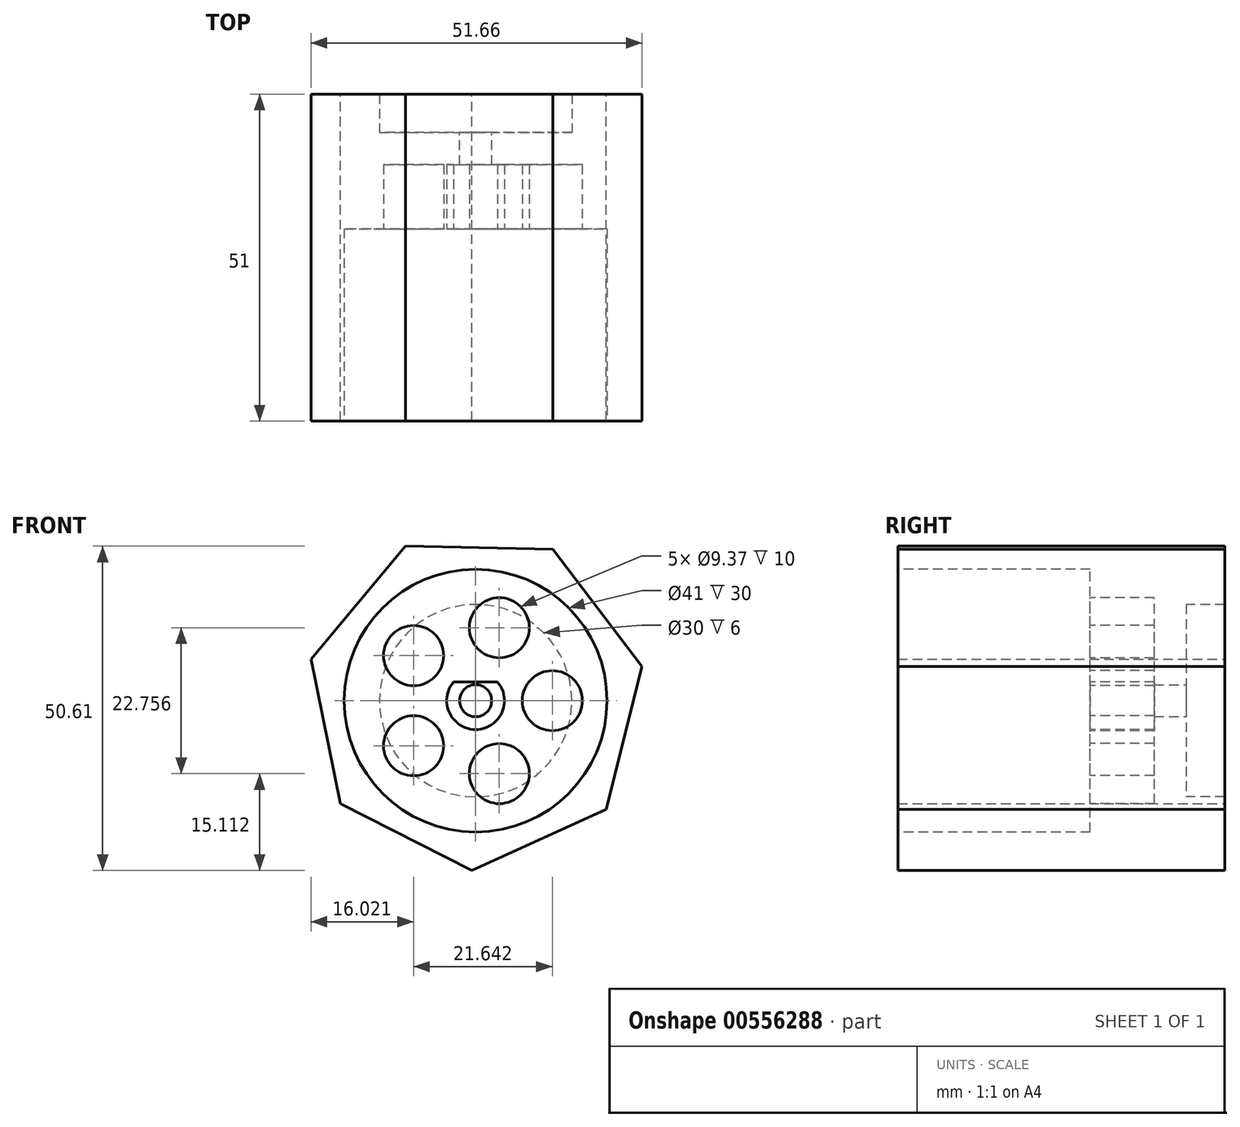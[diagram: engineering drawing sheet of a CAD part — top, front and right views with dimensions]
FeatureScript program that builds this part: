
annotation { "Feature Type Name" : "Feature", "Feature Type Description" : "" }
export const myFeature = defineFeature(function(context is Context, id is Id, definition is map)
    precondition{}
    {
        {
            var Q0;
            Q0=qCreatedBy(makeId("Front.planeOp"),FACE);
            var sketch = newSketch(context, id + "F0", { "sketchPlane" : qUnion([Q0])});
            skCircle(sketch, "E0", {"center": v(0, 0) * mm, "radius": 26.5 * mm});
            skSolve(sketch);
        }
        {
            var Q0;
            Q0 = qSketchRegion(id + "F0", true);
            extrude(context, id + "F1", {"entities" : qUnion([Q0]), "depth" : 45 * mm, "offsetDistance" : 25 * mm});
        }
        {
            var Q0;
            Q0=makeQuery(id+"F1.opExtrude","CAP_FACE",FACE,{"disambiguationData":[OSD([sQuery(id+"F0.wireOp",EDGE,"E0")])],"isStart":false});
            var sketch = newSketch(context, id + "F2", { "sketchPlane" : qUnion([Q0])});
            skCircle(sketch, "E1", {"center": v(0, 0) * mm, "radius": 20.5 * mm});
            skSolve(sketch);
        }
        {
            var Q0;
            Q0 = qSketchRegion(id + "F2", true);
            extrude(context, id + "F3", {"entities" : qUnion([Q0]), "operationType" : NewBodyOperationType.REMOVE, "oppositeDirection" : true, "depth" : 30 * mm, "offsetDistance" : 25 * mm});
        }
        {
            var Q0;
            Q0=makeQuery(id+"F1.opExtrude","CAP_FACE",FACE,{"disambiguationData":[OSD([sQuery(id+"F0.wireOp",EDGE,"E0")])],"isStart":true});
            var sketch = newSketch(context, id + "F4", { "sketchPlane" : qUnion([Q0])});
            skCircle(sketch, "E2", {"center": v(0, 0) * mm, "radius": 2.5 * mm});
            skSolve(sketch);
        }
        {
            var Q0;
            Q0 = qSketchRegion(id + "F4", true);
            extrude(context, id + "F5", {"entities" : qUnion([Q0]), "operationType" : NewBodyOperationType.REMOVE, "endBound" : BoundingType.THROUGH_ALL, "oppositeDirection" : true, "depth" : 25 * mm, "offsetDistance" : 25 * mm});
        }
        {
            var Q0;
            Q0=makeQuery(id+"F3.boolean.opBoolean","COPY",FACE,{"derivedFrom":makeQuery(id+"F3.opExtrude","CAP_FACE",FACE,{"disambiguationData":[OSD([sQuery(id+"F2.wireOp",EDGE,"E1")])],"isStart":false})});
            var sketch = newSketch(context, id + "F6", { "sketchPlane" : qUnion([Q0])});
            skArc(sketch, "E3", {"start": v(-3.43, 2.92) * mm, "mid": v(0, -4.5) * mm, "end": v(3.43, 2.92) * mm});
            skLineSegment(sketch, "E4.bottom", {"start": v(-3.43, 2.92) * mm, "end": v(3.43, 2.92) * mm});
            skPoint(sketch, "E4.middle", {"position": v(0, 4.5) * mm});
            skPoint(sketch, "E4.left.end.orphan", {"position": v(-4, 6.08) * mm});
            skPoint(sketch, "E4.right.end.orphan", {"position": v(4, 6.08) * mm});
            skPoint(sketch, "E5.orphan", {"position": v(4, 2.92) * mm});
            skPoint(sketch, "E6.orphan", {"position": v(-4, 2.92) * mm});
            skSolve(sketch);
        }
        {
            var Q0;
            Q0 = qSketchRegion(id + "F6", true);
            extrude(context, id + "F7", {"entities" : qUnion([Q0]), "operationType" : NewBodyOperationType.REMOVE, "oppositeDirection" : true, "depth" : 10 * mm, "offsetDistance" : 25 * mm});
        }
        {
            var Q0;
            Q0=makeQuery(id+"F1.opExtrude","CAP_FACE",FACE,{"disambiguationData":[OSD([sQuery(id+"F0.wireOp",EDGE,"E0")])],"isStart":true});
            var sketch = newSketch(context, id + "F8", { "sketchPlane" : qUnion([Q0])});
            skCircle(sketch, "E7.cCircle", {"center": v(0, 0) * mm, "radius": 26.5 * mm, "construction": true});
            skLineSegment(sketch, "E7.0", {"start": v(-12.02, 23.62) * mm, "end": v(10.97, 24.12) * mm});
            skLineSegment(sketch, "E7.1", {"start": v(10.97, 24.12) * mm, "end": v(25.7, 6.47) * mm});
            skLineSegment(sketch, "E7.2", {"start": v(25.7, 6.47) * mm, "end": v(21.08, -16.06) * mm});
            skLineSegment(sketch, "E7.3", {"start": v(21.08, -16.06) * mm, "end": v(0.58, -26.5) * mm});
            skLineSegment(sketch, "E7.4", {"start": v(0.58, -26.5) * mm, "end": v(-20.35, -16.98) * mm});
            skLineSegment(sketch, "E7.5", {"start": v(-20.35, -16.98) * mm, "end": v(-25.96, 5.33) * mm});
            skLineSegment(sketch, "E7.6", {"start": v(-25.96, 5.33) * mm, "end": v(-12.02, 23.62) * mm});
            skSolve(sketch);
        }
        {
            var Q0;
            {var subQ0=sQuery(id+"F8.wireOp",EDGE,"E7.6");Q0=makeQuery(id+"F8.imprint","IMPRINT",FACE,{"disambiguationData":[TD([[makeQuery(id+"F8.imprint","IMPRINT",EDGE,{"derivedFrom":subQ0}),1.0]])]});}
            var Q1;
            {var subQ0=sQuery(id+"F8.wireOp",EDGE,"E7.0");Q1=makeQuery(id+"F8.imprint","IMPRINT",FACE,{"disambiguationData":[TD([[makeQuery(id+"F8.imprint","IMPRINT",EDGE,{"derivedFrom":subQ0}),1.0]])]});}
            var Q2;
            {var subQ0=sQuery(id+"F8.wireOp",EDGE,"E7.1");Q2=makeQuery(id+"F8.imprint","IMPRINT",FACE,{"disambiguationData":[TD([[makeQuery(id+"F8.imprint","IMPRINT",EDGE,{"derivedFrom":subQ0}),1.0]])]});}
            var Q3;
            {var subQ0=sQuery(id+"F8.wireOp",EDGE,"E7.2");Q3=makeQuery(id+"F8.imprint","IMPRINT",FACE,{"disambiguationData":[TD([[makeQuery(id+"F8.imprint","IMPRINT",EDGE,{"derivedFrom":subQ0}),1.0]])]});}
            var Q4;
            {var subQ0=sQuery(id+"F8.wireOp",EDGE,"E7.3");Q4=makeQuery(id+"F8.imprint","IMPRINT",FACE,{"disambiguationData":[TD([[makeQuery(id+"F8.imprint","IMPRINT",EDGE,{"derivedFrom":subQ0}),1.0]])]});}
            var Q5;
            {var subQ0=sQuery(id+"F8.wireOp",EDGE,"E7.4");Q5=makeQuery(id+"F8.imprint","IMPRINT",FACE,{"disambiguationData":[TD([[makeQuery(id+"F8.imprint","IMPRINT",EDGE,{"derivedFrom":subQ0}),1.0]])]});}
            var Q6;
            {var subQ0=sQuery(id+"F8.wireOp",EDGE,"E7.5");Q6=makeQuery(id+"F8.imprint","IMPRINT",FACE,{"disambiguationData":[TD([[makeQuery(id+"F8.imprint","IMPRINT",EDGE,{"derivedFrom":subQ0}),1.0]])]});}
            extrude(context, id + "F9", {"entities" : qUnion([Q0, Q1, Q2, Q3, Q4, Q5, Q6]), "operationType" : NewBodyOperationType.REMOVE, "endBound" : BoundingType.THROUGH_ALL, "oppositeDirection" : true, "depth" : 25 * mm, "offsetDistance" : 25 * mm});
        }
        {
            var Q0;
            Q0=makeQuery(id+"F1.opExtrude","CAP_FACE",FACE,{"disambiguationData":[OSD([sQuery(id+"F0.wireOp",EDGE,"E0")])],"isStart":true});
            var sketch = newSketch(context, id + "F10", { "sketchPlane" : qUnion([Q0])});
            skCircle(sketch, "E8", {"center": v(0, 0) * mm, "radius": 15 * mm});
            skSolve(sketch);
        }
        {
            var Q0;
            Q0=makeQuery(id+"F10.imprint","IMPRINT",FACE,{"disambiguationData":[TD([[makeQuery(id+"F10.imprint","IMPRINT",EDGE,{"derivedFrom":sQuery(id+"F10.wireOp",EDGE,"E8")}),-1.0]])]});
            extrude(context, id + "F11", {"entities" : qUnion([Q0]), "operationType" : NewBodyOperationType.ADD, "depth" : 6 * mm, "offsetDistance" : 25 * mm});
        }
        {
            var Q0;
            Q0=makeQuery(id+"F3.boolean.opBoolean","COPY",FACE,{"derivedFrom":makeQuery(id+"F3.opExtrude","CAP_FACE",FACE,{"disambiguationData":[OSD([sQuery(id+"F2.wireOp",EDGE,"E1")])],"isStart":false})});
            var sketch = newSketch(context, id + "F12", { "sketchPlane" : qUnion([Q0])});
            skCircle(sketch, "E9", {"center": v(11.96, 0) * mm, "radius": 4.68 * mm});
            skCircle(sketch, "E10.1.0", {"center": v(3.7, 11.38) * mm, "radius": 4.68 * mm});
            skCircle(sketch, "E10.2.0", {"center": v(-9.68, 7.03) * mm, "radius": 4.68 * mm});
            skCircle(sketch, "E10.3.0", {"center": v(-9.68, -7.03) * mm, "radius": 4.68 * mm});
            skCircle(sketch, "E10.4.0", {"center": v(3.7, -11.38) * mm, "radius": 4.68 * mm});
            skPoint(sketch, "E10.center", {"position": v(0, 0) * mm});
            skSolve(sketch);
        }
        {
            var Q0;
            Q0 = qSketchRegion(id + "F12", true);
            extrude(context, id + "F13", {"entities" : qUnion([Q0]), "operationType" : NewBodyOperationType.REMOVE, "oppositeDirection" : true, "depth" : 10 * mm, "offsetDistance" : 25 * mm});
        }
    });
